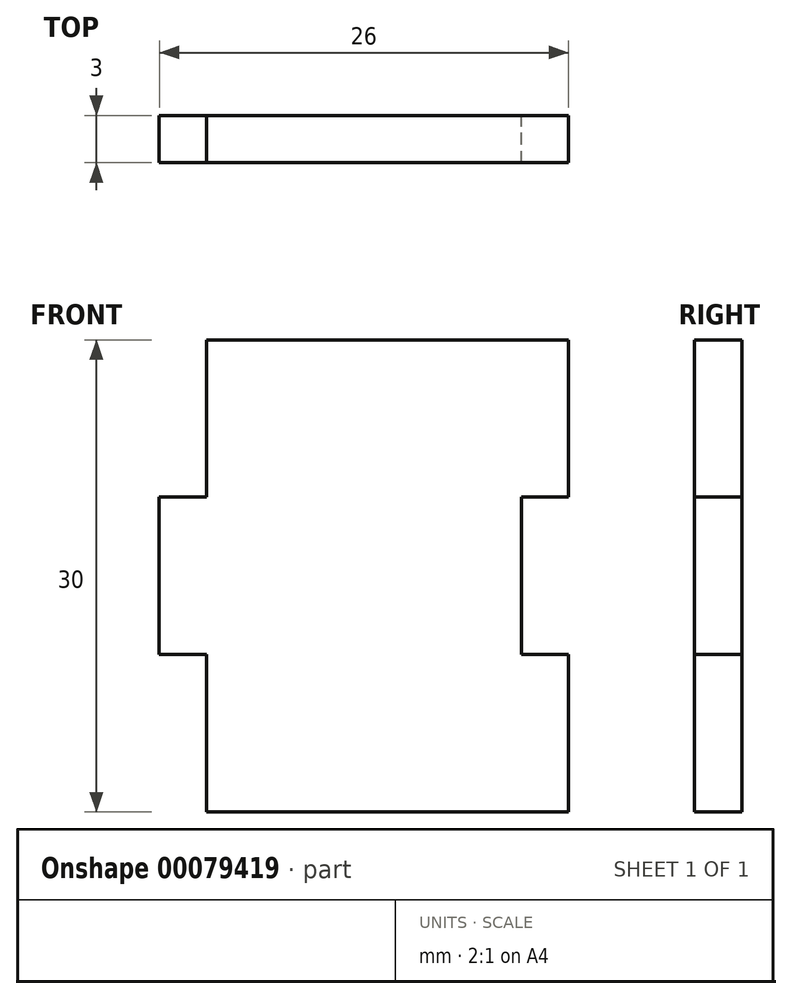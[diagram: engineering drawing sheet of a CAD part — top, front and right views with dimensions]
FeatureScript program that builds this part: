
annotation { "Feature Type Name" : "Feature", "Feature Type Description" : "" }
export const myFeature = defineFeature(function(context is Context, id is Id, definition is map)
    precondition{}
    {
        {
            var Q0;
            Q0=qCreatedBy(makeId("Top.planeOp"),FACE);
            var sketch = newSketch(context, id + "F0", { "sketchPlane" : qUnion([Q0])});
            skLineSegment(sketch, "E0.bottom", {"start": v(0.3, 1.7) * mm, "end": v(20.3, 1.7) * mm});
            skLineSegment(sketch, "E0.top", {"start": v(0.3, -1.3) * mm, "end": v(20.3, -1.3) * mm});
            skLineSegment(sketch, "E0.left", {"start": v(0.3, 1.7) * mm, "end": v(0.3, -1.3) * mm});
            skLineSegment(sketch, "E0.right", {"start": v(20.3, 1.7) * mm, "end": v(20.3, -1.3) * mm});
            skSolve(sketch);
        }
        {
            var Q0;
            Q0=makeQuery(id+"F0.imprint","IMPRINT",FACE,{"disambiguationData":[TD([[makeQuery(id+"F0.imprint","IMPRINT",EDGE,{"derivedFrom":sQuery(id+"F0.wireOp",EDGE,"E0.bottom")}),-1.0]])]});
            extrude(context, id + "F1", {"entities" : qUnion([Q0]), "depth" : 30 * mm});
        }
        {
            var Q0;
            Q0=makeQuery(id+"F1.opExtrude","SWEPT_FACE",FACE,{"disambiguationData":[OSD([sQuery(id+"F0.wireOp",EDGE,"E0.right")])]});
            var sketch = newSketch(context, id + "F2", { "sketchPlane" : qUnion([Q0])});
            skLineSegment(sketch, "E1.bottom", {"start": v(-1.3, 30) * mm, "end": v(1.7, 30) * mm});
            skLineSegment(sketch, "E1.top", {"start": v(-1.3, 20) * mm, "end": v(1.7, 20) * mm});
            skLineSegment(sketch, "E1.left", {"start": v(-1.3, 30) * mm, "end": v(-1.3, 20) * mm});
            skLineSegment(sketch, "E1.right", {"start": v(1.7, 30) * mm, "end": v(1.7, 20) * mm});
            skLineSegment(sketch, "E2.top", {"start": v(-1.3, 10) * mm, "end": v(1.7, 10) * mm});
            skLineSegment(sketch, "E2.left", {"start": v(-1.3, 20) * mm, "end": v(-1.3, 10) * mm});
            skLineSegment(sketch, "E2.right", {"start": v(1.7, 20) * mm, "end": v(1.7, 10) * mm});
            skLineSegment(sketch, "E3.top", {"start": v(-1.3, 0) * mm, "end": v(1.7, 0) * mm});
            skLineSegment(sketch, "E3.left", {"start": v(-1.3, 10) * mm, "end": v(-1.3, 0) * mm});
            skLineSegment(sketch, "E3.right", {"start": v(1.7, 10) * mm, "end": v(1.7, 0) * mm});
            skSolve(sketch);
        }
        {
            var Q0;
            Q0=makeQuery(id+"F2.imprint","IMPRINT",FACE,{"disambiguationData":[TD([[makeQuery(id+"F2.imprint","IMPRINT",EDGE,{"derivedFrom":sQuery(id+"F2.wireOp",EDGE,"E1.bottom")}),1.0]])]});
            var Q1;
            Q1=makeQuery(id+"F2.imprint","IMPRINT",FACE,{"disambiguationData":[TD([[makeQuery(id+"F2.imprint","IMPRINT",EDGE,{"derivedFrom":sQuery(id+"F2.wireOp",EDGE,"E2.top")}),-1.0]])]});
            extrude(context, id + "F3", {"entities" : qUnion([Q0, Q1]), "operationType" : NewBodyOperationType.ADD, "depth" : 3 * mm});
        }
        {
            var Q0;
            Q0=makeQuery(id+"F1.opExtrude","SWEPT_FACE",FACE,{"disambiguationData":[OSD([sQuery(id+"F0.wireOp",EDGE,"E0.left")])]});
            var sketch = newSketch(context, id + "F4", { "sketchPlane" : qUnion([Q0])});
            skLineSegment(sketch, "E4.bottom", {"start": v(-1.7, 30) * mm, "end": v(1.3, 30) * mm});
            skLineSegment(sketch, "E4.top", {"start": v(-1.7, 20) * mm, "end": v(1.3, 20) * mm});
            skLineSegment(sketch, "E4.left", {"start": v(-1.7, 30) * mm, "end": v(-1.7, 20) * mm});
            skLineSegment(sketch, "E4.right", {"start": v(1.3, 30) * mm, "end": v(1.3, 20) * mm});
            skLineSegment(sketch, "E5.top", {"start": v(-1.7, 10) * mm, "end": v(1.3, 10) * mm});
            skLineSegment(sketch, "E5.left", {"start": v(-1.7, 20) * mm, "end": v(-1.7, 10) * mm});
            skLineSegment(sketch, "E5.right", {"start": v(1.3, 20) * mm, "end": v(1.3, 10) * mm});
            skSolve(sketch);
        }
        {
            var Q0;
            Q0=makeQuery(id+"F4.imprint","IMPRINT",FACE,{"disambiguationData":[TD([[makeQuery(id+"F4.imprint","IMPRINT",EDGE,{"derivedFrom":sQuery(id+"F4.wireOp",EDGE,"E4.top")}),-1.0]])]});
            extrude(context, id + "F5", {"entities" : qUnion([Q0]), "operationType" : NewBodyOperationType.ADD, "depth" : 3 * mm});
        }
    });
